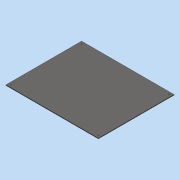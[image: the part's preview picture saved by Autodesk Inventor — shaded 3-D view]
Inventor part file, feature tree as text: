
AUTODESK INVENTOR PART (.ipt)
format: ipt  version: 2016 (Build 200138000, 138)  size: 94,208 bytes
history: native  units: mm
features: hole x4, extrude x1, sketch x1
ambient origin geometry x8: Origin, YZ Plane, XZ Plane, XY Plane, X Axis, Y Axis, Z Axis, Center Point
bodies: Solid1 (feature_tree)
feature tree (6):
  extrude  "Extrusion1"  Depth=360.0mm
  hole  "Hole1"  [1 undecoded]
  hole  "Hole2"  [1 undecoded]
  hole  "Hole3"  [1 undecoded]
  hole  "Hole4"  [1 undecoded]
  sketch  "Sketch1"  dims[d0=440.0mm d1=360.0mm d2=3.0mm d3=0.0mm d4=12.0mm d5=12.0mm d6=4.0mm d7=6.0mm d8=4.0mm d9=2.0mm d10=90.0deg d11=8.0mm d12=20.594885mm d13=12.0mm d14=12.0mm d15=4.0mm d16=6.0mm d17=4.0mm d18=2.0mm d19=90.0deg d20=8.0mm d21=20.594885mm d22=12.0mm d23=12.0mm d24=4.0mm d25=6.0mm d26=4.0mm d27=2.0mm d28=90.0deg d29=8.0mm d30=20.594885mm d31=12.0mm d32=12.0mm d33=4.0mm d34=6.0mm d35=4.0mm d36=2.0mm d37=90.0deg d38=8.0mm d39=20.594885mm]
note: 4 required parameter values undecoded (feature->parameter linkage not recoverable at this tier; creation-order binding heuristic only, values carry confidence <= 0.55)
